# Revit family: xarita s mirror with led lights
name_source: partatom
category: Furniture
units: mm (PartAtom-declared; Revit-internal decimal feet)

## family parameters
Always vertical = Yes
Cut with Voids When Loaded = No
OmniClass Number = 23.40.00.00
OmniClass Title = Equipment and Furnishings
Room Calculation Point = No
Shared = Yes
Work Plane-Based = No

## types (18) — shared parameters
BIMOBJECT = Sanitary: Mirrors
CATALOG = Hansgrohe
COLLECTIONGROUP = Mirrors
DEPTH = 50
DESIGN = Germany
ETIM = EC010550 | Mirror
IFC = Furnishing element
MASTERFORMAT = 08 83 00 | Mirrors
MATERIAL = MATT_WHITE
Manufacturer = Hansgrohe
NBSYN = $BASENUMBER.-$ARTNR.-$MATERIAL.-$LODLEVEL.
NN = Xarita S Mirror with LED lights
OBJECTTYPE = Object (single object)
OMNICLASS = 23-21 37 13 15 | Mirrors
PRODUCTURL = https://pro.hansgrohe.com
UNICLASS2015 = Pr_25_71_53_06 | Bathroom mirrors
UNICLASS_2015_CODE = 25_71_53_06
UNIFORMATII = E2010 | Fixed Furnishings
UNSPSC = 56 | Furniture and Furnishings
etim7_EC010550 = EC010550

## per-type parameters (varying)
| type | ARTNR | BASENUMBER | COLLECTIONSET | GTINCODE | HEIGHT | IDNR | L | LODLEVEL | NAME | PERMALINK | R1 | SPECIFICATION | TYPE | WEIGHT | WIDTH |
| 54981-54981700-MATT_WHITE-200 | 54981700 | 54981 | Xarita S | 4059625463871 | 900 | 1 | 50 | 200 | Xarita S Mirror with LED lights 900/50 capacitive touch sensor | 54981XXX | 450 | Surfaces:    - 54981700 Matt White      Specification:    • material: mirror glass   • material frame: aluminium   • surface material: powder coating   • MoistureProof: durable and splash water resistant material  • SmartTouch: light control via capacitive sensor, sensor switch in the mirror surface  • light source: LED, exchangeable  • direct LED light with 5 different color temperatures gradations  • colour temperature: 2700 - 6500 K  • LED lifetime: > 50.000 hours   • stepless dimmable  • AntiFog: with mirror heating  • Auto-off function: automatic shutdown for all functions   • Memory function: Dimming, color temperature and RGB LED settings  • with mounting material  • concealed fastening  • wall-mounted | C | 7.7 | 900 |
| 54981-54981700-MATT_WHITE-400 | 54981700 | 54981 | Xarita S | 4059625463871 | 900 | 1 | 50 | 400 | Xarita S Mirror with LED lights 900/50 capacitive touch sensor | 54981XXX | 450 | Surfaces:    - 54981700 Matt White      Specification:    • material: mirror glass   • material frame: aluminium   • surface material: powder coating   • MoistureProof: durable and splash water resistant material  • SmartTouch: light control via capacitive sensor, sensor switch in the mirror surface  • light source: LED, exchangeable  • direct LED light with 5 different color temperatures gradations  • colour temperature: 2700 - 6500 K  • LED lifetime: > 50.000 hours   • stepless dimmable  • AntiFog: with mirror heating  • Auto-off function: automatic shutdown for all functions   • Memory function: Dimming, color temperature and RGB LED settings  • with mounting material  • concealed fastening  • wall-mounted | C | 7.7 | 900 |
| 54982-54982700-MATT_WHITE-200 | 54982700 | 54982 | Xarita S | 4059625463864 | 700 | 2 | 50 | 200 | Xarita S Mirror with LED lights 700/50 capacitive touch sensor | 54982XXX | 352 | Surfaces:    - 54982700 Matt White      Specification:    • material: mirror glass   • material frame: aluminium   • surface material: powder coating   • MoistureProof: durable and splash water resistant material  • SmartTouch: light control via capacitive sensor, sensor switch in the mirror surface  • light source: LED, exchangeable  • direct LED light with 5 different color temperatures gradations  • colour temperature: 2700 - 6500 K  • LED lifetime: > 50.000 hours   • stepless dimmable  • AntiFog: with mirror heating  • Auto-off function: automatic shutdown for all functions   • Memory function: Dimming, color temperature and RGB LED settings  • with mounting material  • concealed fastening  • wall-mounted | C | 11.4 | 700 |
| 54982-54982700-MATT_WHITE-400 | 54982700 | 54982 | Xarita S | 4059625463864 | 700 | 2 | 50 | 400 | Xarita S Mirror with LED lights 700/50 capacitive touch sensor | 54982XXX | 352 | Surfaces:    - 54982700 Matt White      Specification:    • material: mirror glass   • material frame: aluminium   • surface material: powder coating   • MoistureProof: durable and splash water resistant material  • SmartTouch: light control via capacitive sensor, sensor switch in the mirror surface  • light source: LED, exchangeable  • direct LED light with 5 different color temperatures gradations  • colour temperature: 2700 - 6500 K  • LED lifetime: > 50.000 hours   • stepless dimmable  • AntiFog: with mirror heating  • Auto-off function: automatic shutdown for all functions   • Memory function: Dimming, color temperature and RGB LED settings  • with mounting material  • concealed fastening  • wall-mounted | C | 11.4 | 700 |
| 54983-54983700-MATT_WHITE-200 | 54983700 | 54983 | Xarita E | 4059625463857 | 706 | 3 | 1606 | 200 | Xarita E Mirror with LED lights 1600/50 capacitive touch sensor | 54983XXX | 706 | Surfaces:    - 54983700 Matt White      Specification:    • material: mirror glass   • material frame: aluminium   • surface material: powder coating   • MoistureProof: durable and splash water resistant material  • SmartTouch: light control via capacitive sensor, sensor switch in the mirror surface  • light source: LED, exchangeable  • direct LED light with 5 different color temperatures gradations  • colour temperature: 2700 - 6500 K  • LED lifetime: > 50.000 hours   • stepless dimmable  • AntiFog: with mirror heating  • Auto-off function: automatic shutdown for all functions   • Memory function: Dimming, color temperature and RGB LED settings  • with mounting material  • concealed fastening  • wall-mounted | R | 16.1 | 1606 |
| 54983-54983700-MATT_WHITE-400 | 54983700 | 54983 | Xarita E | 4059625463857 | 706 | 3 | 1606 | 400 | Xarita E Mirror with LED lights 1600/50 capacitive touch sensor | 54983XXX | 706 | Surfaces:    - 54983700 Matt White      Specification:    • material: mirror glass   • material frame: aluminium   • surface material: powder coating   • MoistureProof: durable and splash water resistant material  • SmartTouch: light control via capacitive sensor, sensor switch in the mirror surface  • light source: LED, exchangeable  • direct LED light with 5 different color temperatures gradations  • colour temperature: 2700 - 6500 K  • LED lifetime: > 50.000 hours   • stepless dimmable  • AntiFog: with mirror heating  • Auto-off function: automatic shutdown for all functions   • Memory function: Dimming, color temperature and RGB LED settings  • with mounting material  • concealed fastening  • wall-mounted | R | 16.1 | 1606 |
| 54984-54984700-MATT_WHITE-200 | 54984700 | 54984 | Xarita E | 4059625463840 | 706 | 4 | 1406 | 200 | Xarita E Mirror with LED lights 1400/50 capacitive touch sensor | 54984XXX | 706 | Surfaces:    - 54984700 Matt White      Specification:    • material: mirror glass   • material frame: aluminium   • surface material: powder coating   • MoistureProof: durable and splash water resistant material  • SmartTouch: light control via capacitive sensor, sensor switch in the mirror surface  • light source: LED, exchangeable  • direct LED light with 5 different color temperatures gradations  • colour temperature: 2700 - 6500 K  • LED lifetime: > 50.000 hours   • stepless dimmable  • AntiFog: with mirror heating  • Auto-off function: automatic shutdown for all functions   • Memory function: Dimming, color temperature and RGB LED settings  • with mounting material  • concealed fastening  • wall-mounted | R | 14.4 | 1406 |
| 54984-54984700-MATT_WHITE-400 | 54984700 | 54984 | Xarita E | 4059625463840 | 706 | 4 | 1406 | 400 | Xarita E Mirror with LED lights 1400/50 capacitive touch sensor | 54984XXX | 706 | Surfaces:    - 54984700 Matt White      Specification:    • material: mirror glass   • material frame: aluminium   • surface material: powder coating   • MoistureProof: durable and splash water resistant material  • SmartTouch: light control via capacitive sensor, sensor switch in the mirror surface  • light source: LED, exchangeable  • direct LED light with 5 different color temperatures gradations  • colour temperature: 2700 - 6500 K  • LED lifetime: > 50.000 hours   • stepless dimmable  • AntiFog: with mirror heating  • Auto-off function: automatic shutdown for all functions   • Memory function: Dimming, color temperature and RGB LED settings  • with mounting material  • concealed fastening  • wall-mounted | R | 14.4 | 1406 |
| 54985-54985700-MATT_WHITE-200 | 54985700 | 54985 | Xarita E | 4059625463833 | 706 | 5 | 1206 | 200 | Xarita E Mirror with LED lights 1200/50 capacitive touch sensor | 54985XXX | 706 | Surfaces:    - 54985700 Matt White      Specification:    • material: mirror glass   • material frame: aluminium   • surface material: powder coating   • MoistureProof: durable and splash water resistant material  • SmartTouch: light control via capacitive sensor, sensor switch in the mirror surface  • light source: LED, exchangeable  • direct LED light with 5 different color temperatures gradations  • colour temperature: 2700 - 6500 K  • LED lifetime: > 50.000 hours   • stepless dimmable  • AntiFog: with mirror heating  • Auto-off function: automatic shutdown for all functions   • Memory function: Dimming, color temperature and RGB LED settings  • with mounting material  • concealed fastening  • wall-mounted | R | 12.6 | 1206 |
| 54985-54985700-MATT_WHITE-400 | 54985700 | 54985 | Xarita E | 4059625463833 | 706 | 5 | 1206 | 400 | Xarita E Mirror with LED lights 1200/50 capacitive touch sensor | 54985XXX | 706 | Surfaces:    - 54985700 Matt White      Specification:    • material: mirror glass   • material frame: aluminium   • surface material: powder coating   • MoistureProof: durable and splash water resistant material  • SmartTouch: light control via capacitive sensor, sensor switch in the mirror surface  • light source: LED, exchangeable  • direct LED light with 5 different color temperatures gradations  • colour temperature: 2700 - 6500 K  • LED lifetime: > 50.000 hours   • stepless dimmable  • AntiFog: with mirror heating  • Auto-off function: automatic shutdown for all functions   • Memory function: Dimming, color temperature and RGB LED settings  • with mounting material  • concealed fastening  • wall-mounted | R | 12.6 | 1206 |
| 54986-54986700-MATT_WHITE-200 | 54986700 | 54986 | Xarita E | 4059625463826 | 706 | 6 | 1006 | 200 | Xarita E Mirror with LED lights 1000/50 capacitive touch sensor | 54986XXX | 706 | Surfaces:    - 54986700 Matt White      Specification:    • material: mirror glass   • material frame: aluminium   • surface material: powder coating   • MoistureProof: durable and splash water resistant material  • SmartTouch: light control via capacitive sensor, sensor switch in the mirror surface  • light source: LED, exchangeable  • direct LED light with 5 different color temperatures gradations  • colour temperature: 2700 - 6500 K  • LED lifetime: > 50.000 hours   • stepless dimmable  • AntiFog: with mirror heating  • Auto-off function: automatic shutdown for all functions   • Memory function: Dimming, color temperature and RGB LED settings  • with mounting material  • concealed fastening  • wall-mounted | R | 10.7 | 1006 |
| 54986-54986700-MATT_WHITE-400 | 54986700 | 54986 | Xarita E | 4059625463826 | 706 | 6 | 1006 | 400 | Xarita E Mirror with LED lights 1000/50 capacitive touch sensor | 54986XXX | 706 | Surfaces:    - 54986700 Matt White      Specification:    • material: mirror glass   • material frame: aluminium   • surface material: powder coating   • MoistureProof: durable and splash water resistant material  • SmartTouch: light control via capacitive sensor, sensor switch in the mirror surface  • light source: LED, exchangeable  • direct LED light with 5 different color temperatures gradations  • colour temperature: 2700 - 6500 K  • LED lifetime: > 50.000 hours   • stepless dimmable  • AntiFog: with mirror heating  • Auto-off function: automatic shutdown for all functions   • Memory function: Dimming, color temperature and RGB LED settings  • with mounting material  • concealed fastening  • wall-mounted | R | 10.7 | 1006 |
| 54987-54987700-MATT_WHITE-200 | 54987700 | 54987 | Xarita E | 4059625463819 | 706 | 7 | 806 | 200 | Xarita E Mirror with LED lights 800/50 capacitive touch sensor | 54987XXX | 706 | Surfaces:    - 54987700 Matt White      Specification:    • material: mirror glass   • material frame: aluminium   • surface material: powder coating   • MoistureProof: durable and splash water resistant material  • SmartTouch: light control via capacitive sensor, sensor switch in the mirror surface  • light source: LED, exchangeable  • direct LED light with 5 different color temperatures gradations  • colour temperature: 2700 - 6500 K  • LED lifetime: > 50.000 hours   • stepless dimmable  • AntiFog: with mirror heating  • Auto-off function: automatic shutdown for all functions   • Memory function: Dimming, color temperature and RGB LED settings  • with mounting material  • concealed fastening  • wall-mounted | R | 9 | 806 |
| 54987-54987700-MATT_WHITE-400 | 54987700 | 54987 | Xarita E | 4059625463819 | 706 | 7 | 806 | 400 | Xarita E Mirror with LED lights 800/50 capacitive touch sensor | 54987XXX | 706 | Surfaces:    - 54987700 Matt White      Specification:    • material: mirror glass   • material frame: aluminium   • surface material: powder coating   • MoistureProof: durable and splash water resistant material  • SmartTouch: light control via capacitive sensor, sensor switch in the mirror surface  • light source: LED, exchangeable  • direct LED light with 5 different color temperatures gradations  • colour temperature: 2700 - 6500 K  • LED lifetime: > 50.000 hours   • stepless dimmable  • AntiFog: with mirror heating  • Auto-off function: automatic shutdown for all functions   • Memory function: Dimming, color temperature and RGB LED settings  • with mounting material  • concealed fastening  • wall-mounted | R | 9 | 806 |
| 54988-54988700-MATT_WHITE-200 | 54988700 | 54988 | Xarita E | 4059625463802 | 706 | 8 | 606 | 200 | Xarita E Mirror with LED lights 600/50 capacitive touch sensor | 54988XXX | 706 | Surfaces:    - 54988700 Matt White      Specification:    • material: mirror glass   • material frame: aluminium   • surface material: powder coating   • MoistureProof: durable and splash water resistant material  • SmartTouch: light control via capacitive sensor, sensor switch in the mirror surface  • light source: LED, exchangeable  • direct LED light with 5 different color temperatures gradations  • colour temperature: 2700 - 6500 K  • LED lifetime: > 50.000 hours   • stepless dimmable  • AntiFog: with mirror heating  • Auto-off function: automatic shutdown for all functions   • Memory function: Dimming, color temperature and RGB LED settings  • with mounting material  • concealed fastening  • wall-mounted | R | 7.2 | 606 |
| 54988-54988700-MATT_WHITE-400 | 54988700 | 54988 | Xarita E | 4059625463802 | 706 | 8 | 606 | 400 | Xarita E Mirror with LED lights 600/50 capacitive touch sensor | 54988XXX | 706 | Surfaces:    - 54988700 Matt White      Specification:    • material: mirror glass   • material frame: aluminium   • surface material: powder coating   • MoistureProof: durable and splash water resistant material  • SmartTouch: light control via capacitive sensor, sensor switch in the mirror surface  • light source: LED, exchangeable  • direct LED light with 5 different color temperatures gradations  • colour temperature: 2700 - 6500 K  • LED lifetime: > 50.000 hours   • stepless dimmable  • AntiFog: with mirror heating  • Auto-off function: automatic shutdown for all functions   • Memory function: Dimming, color temperature and RGB LED settings  • with mounting material  • concealed fastening  • wall-mounted | R | 7.2 | 606 |
| 54989-54989700-MATT_WHITE-200 | 54989700 | 54989 | Xarita E | 4059625463796 | 706 | 9 | 506 | 200 | Xarita E Mirror with LED lights 500/50 capacitive touch sensor | 54989XXX | 706 | Surfaces:    - 54989700 Matt White      Specification:    • material: mirror glass   • material frame: aluminium   • surface material: powder coating   • MoistureProof: durable and splash water resistant material  • SmartTouch: light control via capacitive sensor, sensor switch in the mirror surface  • light source: LED, exchangeable  • direct LED light with 5 different color temperatures gradations  • colour temperature: 2700 - 6500 K  • LED lifetime: > 50.000 hours   • stepless dimmable  • AntiFog: with mirror heating  • Auto-off function: automatic shutdown for all functions   • Memory function: Dimming, color temperature and RGB LED settings  • with mounting material  • concealed fastening  • wall-mounted | R | 6.2 | 506 |
| 54989-54989700-MATT_WHITE-400 | 54989700 | 54989 | Xarita E | 4059625463796 | 706 | 9 | 506 | 400 | Xarita E Mirror with LED lights 500/50 capacitive touch sensor | 54989XXX | 706 | Surfaces:    - 54989700 Matt White      Specification:    • material: mirror glass   • material frame: aluminium   • surface material: powder coating   • MoistureProof: durable and splash water resistant material  • SmartTouch: light control via capacitive sensor, sensor switch in the mirror surface  • light source: LED, exchangeable  • direct LED light with 5 different color temperatures gradations  • colour temperature: 2700 - 6500 K  • LED lifetime: > 50.000 hours   • stepless dimmable  • AntiFog: with mirror heating  • Auto-off function: automatic shutdown for all functions   • Memory function: Dimming, color temperature and RGB LED settings  • with mounting material  • concealed fastening  • wall-mounted | R | 6.2 | 506 |

note: column(s) folded — value = type name in every type: LINA, Model, NB

type visibility flags: 18 boolean params named "<type name>_RX0RY0RZ0TX0TY0TZ0_V" — each type sets only its own to Yes (folded from table)

## geometry (parser evidence)
native form markers: Sweep x49
no freeform markers — native parametric forms only
